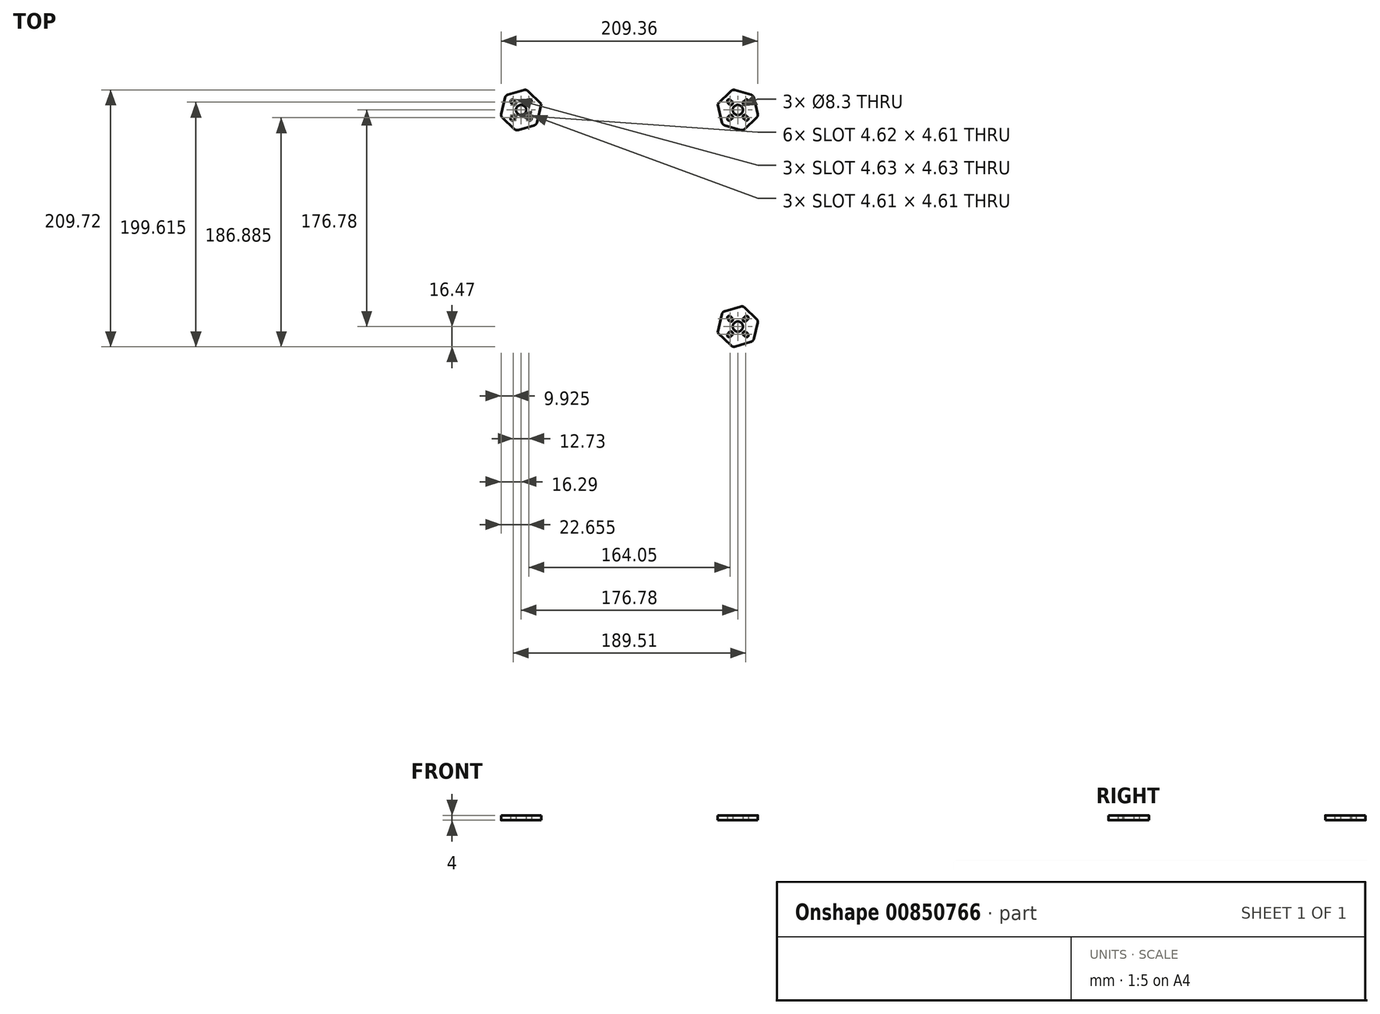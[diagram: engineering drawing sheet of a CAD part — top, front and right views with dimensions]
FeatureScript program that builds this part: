
annotation { "Feature Type Name" : "Feature", "Feature Type Description" : "" }
export const myFeature = defineFeature(function(context is Context, id is Id, definition is map)
    precondition{}
    {
        {
            var Q0;
            Q0=qCreatedBy(makeId("Top.planeOp"),FACE);
            var sketch = newSketch(context, id + "F0", { "sketchPlane" : qUnion([Q0])});
            skCircle(sketch, "E0", {"center": v(15.25, 15.25) * mm, "radius": 1.6 * mm});
            skPoint(sketch, "E1.middle", {"position": v(88.39, 88.39) * mm});
            skLineSegment(sketch, "E2", {"start": v(88.39, 88.39) * mm, "end": v(0, 0) * mm, "construction": true});
            skCircle(sketch, "E3", {"center": v(88.39, 88.39) * mm, "radius": 70 * mm, "construction": true});
            skLineSegment(sketch, "E4.MirrorCS", {"start": v(18.44, 10) * mm, "end": v(18.44, 0) * mm});
            skCircle(sketch, "E5", {"center": v(88.39, 88.39) * mm, "radius": 4.15 * mm});
            skLineSegment(sketch, "E6", {"start": v(5, 29.83) * mm, "end": v(84.33, 105.23) * mm});
            skCircle(sketch, "E7.cCircle", {"center": v(88.39, 88.39) * mm, "radius": 15 * mm, "construction": true});
            skLineSegment(sketch, "E7.0", {"start": v(71.78, 93.3) * mm, "end": v(84.33, 105.23) * mm});
            skLineSegment(sketch, "E7.1", {"start": v(84.33, 105.23) * mm, "end": v(100.94, 100.32) * mm});
            skLineSegment(sketch, "E7.2", {"start": v(100.94, 100.32) * mm, "end": v(105, 83.48) * mm});
            skLineSegment(sketch, "E7.3", {"start": v(105, 83.48) * mm, "end": v(92.44, 71.55) * mm});
            skLineSegment(sketch, "E7.4", {"start": v(92.44, 71.55) * mm, "end": v(75.83, 76.46) * mm});
            skLineSegment(sketch, "E7.5", {"start": v(75.83, 76.46) * mm, "end": v(71.78, 93.3) * mm});
            skPoint(sketch, "E7.0.midPoint", {"position": v(78.05, 99.26) * mm});
            skLineSegment(sketch, "E8", {"start": v(18.44, 0) * mm, "end": v(0, 0) * mm});
            skCircle(sketch, "E9.MirrorC", {"center": v(88.39, -88.39) * mm, "radius": 70 * mm, "construction": true});
            skLineSegment(sketch, "E10", {"start": v(22.44, 10) * mm, "end": v(22.44, 0) * mm});
            skLineSegment(sketch, "E11", {"start": v(22.44, 0) * mm, "end": v(31, 0) * mm});
            skLineSegment(sketch, "E12", {"start": v(31, 0) * mm, "end": v(31, 20) * mm});
            skCircle(sketch, "E13.MirrorC", {"center": v(-88.39, 88.39) * mm, "radius": 70 * mm, "construction": true});
            skCircle(sketch, "E14.MirrorC", {"center": v(-88.39, -88.39) * mm, "radius": 70 * mm, "construction": true});
            skLineSegment(sketch, "E15", {"start": v(22.44, 10) * mm, "end": v(18.44, 10) * mm, "construction": true});
            skArc(sketch, "E16", {"start": v(22.44, 10) * mm, "mid": v(20.44, 12) * mm, "end": v(18.44, 10) * mm});
            skLineSegment(sketch, "E17", {"start": v(5, 29.83) * mm, "end": v(0, 29.83) * mm});
            skLineSegment(sketch, "E18", {"start": v(0, 0) * mm, "end": v(0, 29.83) * mm});
            skCircle(sketch, "E19", {"center": v(28, 17) * mm, "radius": 1.65 * mm});
            skLineSegment(sketch, "E20", {"start": v(28, 17) * mm, "end": v(31, 17) * mm, "construction": true});
            skLineSegment(sketch, "E21", {"start": v(31, 17) * mm, "end": v(31, 20) * mm, "construction": true});
            skLineSegment(sketch, "E22", {"start": v(31, 17) * mm, "end": v(31, 20) * mm});
            skLineSegment(sketch, "E23", {"start": v(4.87, 0) * mm, "end": v(4.87, 10) * mm});
            skLineSegment(sketch, "E24", {"start": v(8.87, 0) * mm, "end": v(8.87, 10) * mm});
            skLineSegment(sketch, "E25", {"start": v(8.87, 10) * mm, "end": v(4.87, 10) * mm, "construction": true});
            skArc(sketch, "E26", {"start": v(8.87, 10) * mm, "mid": v(6.87, 12) * mm, "end": v(4.87, 10) * mm});
            skLineSegment(sketch, "E27", {"start": v(31, 20) * mm, "end": v(36.02, 33.1) * mm});
            skLineSegment(sketch, "E28", {"start": v(36.02, 33.1) * mm, "end": v(80.26, 75.15) * mm});
            skLineSegment(sketch, "E29.bottom", {"start": v(25, 14) * mm, "end": v(31, 14) * mm, "construction": true});
            skLineSegment(sketch, "E29.top", {"start": v(25, 20) * mm, "end": v(31, 20) * mm, "construction": true});
            skLineSegment(sketch, "E29.left", {"start": v(25, 14) * mm, "end": v(25, 20) * mm, "construction": true});
            skLineSegment(sketch, "E29.right", {"start": v(31, 14) * mm, "end": v(31, 20) * mm, "construction": true});
            skLineSegment(sketch, "E30", {"start": v(22.44, 0) * mm, "end": v(18.44, 0) * mm, "construction": true});
            skLineSegment(sketch, "E31", {"start": v(88.39, 88.39) * mm, "end": v(95.46, 81.32) * mm, "construction": true});
            skLineSegment(sketch, "E32", {"start": v(88.39, 88.39) * mm, "end": v(95.46, 95.46) * mm, "construction": true});
            skLineSegment(sketch, "E33", {"start": v(95.46, 95.46) * mm, "end": v(81.32, 81.32) * mm, "construction": true});
            skArc(sketch, "E34", {"start": v(96.6, 94.33) * mm, "mid": v(96.6, 96.6) * mm, "end": v(94.33, 96.6) * mm});
            skLineSegment(sketch, "E35", {"start": v(88.39, 88.39) * mm, "end": v(94.05, 94.05) * mm});
            skArc(sketch, "E36", {"start": v(92.91, 95.18) * mm, "mid": v(92.91, 92.91) * mm, "end": v(95.18, 92.91) * mm});
            skLineSegment(sketch, "E37", {"start": v(94.05, 94.05) * mm, "end": v(95.18, 92.91) * mm, "construction": true});
            skLineSegment(sketch, "E38", {"start": v(95.46, 95.46) * mm, "end": v(96.6, 94.33) * mm, "construction": true});
            skLineSegment(sketch, "E39", {"start": v(96.6, 94.33) * mm, "end": v(94.33, 96.6) * mm, "construction": true});
            skLineSegment(sketch, "E40", {"start": v(94.05, 94.05) * mm, "end": v(92.91, 95.18) * mm, "construction": true});
            skLineSegment(sketch, "E41", {"start": v(94.33, 96.6) * mm, "end": v(92.91, 95.18) * mm});
            skLineSegment(sketch, "E42", {"start": v(96.6, 94.33) * mm, "end": v(95.18, 92.91) * mm});
            skLineSegment(sketch, "E43", {"start": v(88.39, 88.39) * mm, "end": v(98.48, 88.39) * mm, "construction": true});
            skLineSegment(sketch, "E44", {"start": v(88.39, 88.39) * mm, "end": v(82.4, 88.39) * mm, "construction": true});
            skLineSegment(sketch, "E45", {"start": v(88.39, 88.39) * mm, "end": v(88.39, 82.43) * mm, "construction": true});
            skArc(sketch, "E46.MirrorCS", {"start": v(92.91, 81.6) * mm, "mid": v(92.91, 83.86) * mm, "end": v(95.18, 83.86) * mm});
            skArc(sketch, "E47.MirrorCS", {"start": v(96.6, 82.45) * mm, "mid": v(96.6, 80.19) * mm, "end": v(94.33, 80.19) * mm});
            skLineSegment(sketch, "E48.MirrorCS", {"start": v(94.33, 80.19) * mm, "end": v(92.91, 81.6) * mm});
            skLineSegment(sketch, "E49.MirrorCS", {"start": v(94.05, 82.73) * mm, "end": v(92.91, 81.6) * mm, "construction": true});
            skLineSegment(sketch, "E50.MirrorCS", {"start": v(95.46, 81.32) * mm, "end": v(96.6, 82.45) * mm, "construction": true});
            skLineSegment(sketch, "E51.MirrorCS", {"start": v(94.05, 82.73) * mm, "end": v(95.18, 83.86) * mm, "construction": true});
            skLineSegment(sketch, "E52.MirrorCS", {"start": v(96.6, 82.45) * mm, "end": v(94.33, 80.19) * mm, "construction": true});
            skLineSegment(sketch, "E53.MirrorCS", {"start": v(96.6, 82.45) * mm, "end": v(95.18, 83.86) * mm});
            skLineSegment(sketch, "E54.MirrorCS", {"start": v(80.19, 82.45) * mm, "end": v(81.6, 83.86) * mm});
            skLineSegment(sketch, "E55.MirrorCS", {"start": v(82.45, 80.19) * mm, "end": v(83.86, 81.6) * mm});
            skArc(sketch, "E56.MirrorCS", {"start": v(80.19, 82.45) * mm, "mid": v(80.19, 80.19) * mm, "end": v(82.45, 80.19) * mm});
            skArc(sketch, "E57.MirrorCS", {"start": v(83.86, 81.6) * mm, "mid": v(83.86, 83.86) * mm, "end": v(81.6, 83.86) * mm});
            skLineSegment(sketch, "E58.MirrorCS", {"start": v(80.19, 94.33) * mm, "end": v(81.6, 92.91) * mm});
            skLineSegment(sketch, "E59.MirrorCS", {"start": v(82.45, 96.6) * mm, "end": v(83.86, 95.18) * mm});
            skArc(sketch, "E60.MirrorCS", {"start": v(83.86, 95.18) * mm, "mid": v(83.86, 92.91) * mm, "end": v(81.6, 92.91) * mm});
            skArc(sketch, "E61.MirrorCS", {"start": v(80.19, 94.33) * mm, "mid": v(80.19, 96.6) * mm, "end": v(82.45, 96.6) * mm});
            skSolve(sketch);
        }
        {
            var Q0;
            Q0=makeQuery(id+"F0.imprint","IMPRINT",FACE,{"disambiguationData":[TD([[makeQuery(id+"F0.imprint","IMPRINT",EDGE,{"derivedFrom":sQuery(id+"F0.wireOp",EDGE,"E0")}),-1.0]])]});
            var Q1;
            Q1=makeQuery(id+"F0.imprint","IMPRINT",FACE,{"disambiguationData":[TD([[makeQuery(id+"F0.imprint","IMPRINT",EDGE,{"derivedFrom":sQuery(id+"F0.wireOp",EDGE,"a8402e06-ee66-4db1-b534-accf88d6755370.MirrorCS")}),1.0]])]});
            var Q2;
            Q2=makeQuery(id+"F0.imprint","IMPRINT",FACE,{"disambiguationData":[TD([[makeQuery(id+"F0.imprint","IMPRINT",EDGE,{"derivedFrom":sQuery(id+"F0.wireOp",EDGE,"E7.0")}),-1.0]])]});
            extrude(context, id + "F1", {"entities" : qUnion([Q0, Q1, Q2]), "depth" : 4 * mm, "offsetDistance" : 25 * mm});
        }
        {
            var Q0;
            Q0=makeQuery(id+"F1.opExtrude","SWEPT_EDGE",EDGE,{"disambiguationData":[OSD([sQuery(id+"F0.wireOp",EDGE,"E4.MirrorCS"),sQuery(id+"F0.wireOp",EDGE,"E16")])]});
            var Q1;
            Q1=makeQuery(id+"F1.opExtrude","SWEPT_EDGE",EDGE,{"disambiguationData":[OSD([sQuery(id+"F0.wireOp",EDGE,"cHvUN8nU-x71g-40xa-NfZp-NOtcJyjpFuAi"),sQuery(id+"F0.wireOp",EDGE,"epl4RrYL-OSQW-atUW-LyBx-qaYWwqfy6PMm")])]});
            var Q2;
            Q2=makeQuery(id+"F1.opExtrude","SWEPT_EDGE",EDGE,{"disambiguationData":[OSD([sQuery(id+"F0.wireOp",EDGE,"cHvUN8nU-x71g-40xa-NfZp-NOtcJyjpFuAi"),sQuery(id+"F0.wireOp",EDGE,"E7.4")])]});
            var Q3;
            Q3=makeQuery(id+"F1.opExtrude","SWEPT_EDGE",EDGE,{"disambiguationData":[OSD([sQuery(id+"F0.wireOp",EDGE,"E7.3"),sQuery(id+"F0.wireOp",EDGE,"E7.4")])]});
            var Q4;
            Q4=makeQuery(id+"F1.opExtrude","SWEPT_EDGE",EDGE,{"disambiguationData":[OSD([sQuery(id+"F0.wireOp",EDGE,"E7.2"),sQuery(id+"F0.wireOp",EDGE,"E7.3")])]});
            var Q5;
            Q5=makeQuery(id+"F1.opExtrude","SWEPT_EDGE",EDGE,{"disambiguationData":[OSD([sQuery(id+"F0.wireOp",EDGE,"E7.1"),sQuery(id+"F0.wireOp",EDGE,"E7.2")])]});
            var Q6;
            Q6=makeQuery(id+"F1.opExtrude","SWEPT_EDGE",EDGE,{"disambiguationData":[OSD([sQuery(id+"F0.wireOp",EDGE,"E7.0"),sQuery(id+"F0.wireOp",EDGE,"E7.1")])]});
            var Q7;
            Q7=makeQuery(id+"F1.opExtrude","SWEPT_EDGE",EDGE,{"disambiguationData":[OSD([sQuery(id+"F0.wireOp",EDGE,"E6"),sQuery(id+"F0.wireOp",EDGE,"E17")])]});
            var Q8;
            Q8=makeQuery(id+"F1.opExtrude","SWEPT_EDGE",EDGE,{"disambiguationData":[OSD([sQuery(id+"F0.wireOp",EDGE,"E27"),sQuery(id+"F0.wireOp",EDGE,"E28")])]});
            fillet(context, id + "F2", {"entities" : qUnion([Q0, Q1, Q2, Q3, Q4, Q5, Q6, Q7, Q8]), "radius" : 3 * mm, "tangentPropagation" : true, "allowEdgeOverflow" : false});
        }
        {
            var Q0;
            Q0=makeQuery(id+"F1.opExtrude","SWEPT_BODY",BODY,{"disambiguationData":[OSD([sQuery(id+"F0.wireOp",EDGE,"E0"),sQuery(id+"F0.wireOp",EDGE,"oWdG6ISu-KMsr-k3RM-oKNs-BBQdvasnS4HI"),sQuery(id+"F0.wireOp",EDGE,"5BciHUZ9-YItP-bftD-ryj1-fLEm0wkKDPWy"),sQuery(id+"F0.wireOp",EDGE,"IMcl1Ms8-7Su7-6ZAW-NG62-JrzNrDPbqV1x"),sQuery(id+"F0.wireOp",EDGE,"9lDLXxTV-PYSm-tJxw-fFQl-kT38rdbVkR7x"),sQuery(id+"F0.wireOp",EDGE,"BTfzHgYM-Pcws-li4g-SYp3-UJARv1mQOSm9"),sQuery(id+"F0.wireOp",EDGE,"db9e6dd7-a62a-4760-a6cd-ab0fbc12ccb50.MirrorCS"),sQuery(id+"F0.wireOp",EDGE,"E4.MirrorCS"),sQuery(id+"F0.wireOp",EDGE,"E5"),sQuery(id+"F0.wireOp",EDGE,"cHvUN8nU-x71g-40xa-NfZp-NOtcJyjpFuAi"),sQuery(id+"F0.wireOp",EDGE,"0RzsWIGJ-paQ4-ph2x-eddI-tqWgFJrQCAKC"),sQuery(id+"F0.wireOp",EDGE,"a8402e06-ee66-4db1-b534-accf88d6755370.MirrorCS"),sQuery(id+"F0.wireOp",EDGE,"b02bcf13-f754-48f6-a3d9-f9d052b593f50.MirrorCS"),sQuery(id+"F0.wireOp",EDGE,"694f7e91-0505-4e5e-88bd-36493d61fdc10.MirrorCS"),sQuery(id+"F0.wireOp",EDGE,"c5342205-c0ba-4404-b584-cfb84c0711390.MirrorCS"),sQuery(id+"F0.wireOp",EDGE,"41230d2a-ef97-414e-a6b5-391d20fd2f8c0.MirrorCS"),sQuery(id+"F0.wireOp",EDGE,"f38d681c-4026-4150-9bb3-d62f81ecb60f0.MirrorCS"),sQuery(id+"F0.wireOp",EDGE,"f9c18b0d-e090-48c1-8617-159294224c630.MirrorCS"),sQuery(id+"F0.wireOp",EDGE,"00e02f4d-f463-4009-913d-c35542a66ec00.MirrorCS"),sQuery(id+"F0.wireOp",EDGE,"3930c83d-3c26-45a6-b419-dbd5f18dbc8c0.MirrorCS"),sQuery(id+"F0.wireOp",EDGE,"795dee3e-9adc-4518-a6c0-085d1af0c0d60.MirrorCS"),sQuery(id+"F0.wireOp",EDGE,"679d401b-33ac-4602-9026-ff56514631890.MirrorCS"),sQuery(id+"F0.wireOp",EDGE,"5c1dbbd6-dfe0-41fd-a57b-e75cf78051b50.MirrorCS"),sQuery(id+"F0.wireOp",EDGE,"7f1d194b-443a-46c3-ae38-eac5abfad72a0.MirrorCS"),sQuery(id+"F0.wireOp",EDGE,"7f1d194b-443a-46c3-ae38-eac5abfad72a1.MirrorCS"),sQuery(id+"F0.wireOp",EDGE,"7f1d194b-443a-46c3-ae38-eac5abfad72a2.MirrorCS"),sQuery(id+"F0.wireOp",EDGE,"7f1d194b-443a-46c3-ae38-eac5abfad72a3.MirrorCS"),sQuery(id+"F0.wireOp",EDGE,"7f1d194b-443a-46c3-ae38-eac5abfad72a4.MirrorCS"),sQuery(id+"F0.wireOp",EDGE,"7f1d194b-443a-46c3-ae38-eac5abfad72a5.MirrorCS"),sQuery(id+"F0.wireOp",EDGE,"9a7043b3-dbb6-42aa-b538-a97c510add320.MirrorCS"),sQuery(id+"F0.wireOp",EDGE,"9a7043b3-dbb6-42aa-b538-a97c510add321.MirrorCS"),sQuery(id+"F0.wireOp",EDGE,"9a7043b3-dbb6-42aa-b538-a97c510add322.MirrorCS"),sQuery(id+"F0.wireOp",EDGE,"9a7043b3-dbb6-42aa-b538-a97c510add323.MirrorCS"),sQuery(id+"F0.wireOp",EDGE,"9a7043b3-dbb6-42aa-b538-a97c510add324.MirrorCS"),sQuery(id+"F0.wireOp",EDGE,"9a7043b3-dbb6-42aa-b538-a97c510add325.MirrorCS"),sQuery(id+"F0.wireOp",EDGE,"FqZT0Coj-QeVh-UZiT-ubz3-8URiVkSl8LEo"),sQuery(id+"F0.wireOp",EDGE,"E6"),sQuery(id+"F0.wireOp",EDGE,"E7.0"),sQuery(id+"F0.wireOp",EDGE,"E7.1"),sQuery(id+"F0.wireOp",EDGE,"E7.2"),sQuery(id+"F0.wireOp",EDGE,"E7.3"),sQuery(id+"F0.wireOp",EDGE,"E7.4"),sQuery(id+"F0.wireOp",EDGE,"sgrcP4Hu-TaEZ-ddCh-wFjH-NDSiAUyIGktv"),sQuery(id+"F0.wireOp",EDGE,"yxbqhxj4-Hobq-MuBO-747H-CFA98GxcXYLo"),sQuery(id+"F0.wireOp",EDGE,"E8"),sQuery(id+"F0.wireOp",EDGE,"GbNPMmSl-UyhI-VWxR-HjZI-7ZSacyFRmm5m"),sQuery(id+"F0.wireOp",EDGE,"380TYFXR-L58P-DwUR-NOKN-1QwqNV3a178d")])]});
            var Q1;
            Q1=qCreatedBy(makeId("Right.planeOp"),FACE);
            mirror(context, id + "F3", {"operationType" : NewBodyOperationType.ADD, "entities" : qUnion([Q0]), "mirrorPlane" : qUnion([Q1])});
        }
        {
            var Q0;
            Q0=makeQuery(id+"F1.opExtrude","SWEPT_BODY",BODY,{"disambiguationData":[OSD([sQuery(id+"F0.wireOp",EDGE,"E0"),sQuery(id+"F0.wireOp",EDGE,"oWdG6ISu-KMsr-k3RM-oKNs-BBQdvasnS4HI"),sQuery(id+"F0.wireOp",EDGE,"5BciHUZ9-YItP-bftD-ryj1-fLEm0wkKDPWy"),sQuery(id+"F0.wireOp",EDGE,"IMcl1Ms8-7Su7-6ZAW-NG62-JrzNrDPbqV1x"),sQuery(id+"F0.wireOp",EDGE,"9lDLXxTV-PYSm-tJxw-fFQl-kT38rdbVkR7x"),sQuery(id+"F0.wireOp",EDGE,"BTfzHgYM-Pcws-li4g-SYp3-UJARv1mQOSm9"),sQuery(id+"F0.wireOp",EDGE,"db9e6dd7-a62a-4760-a6cd-ab0fbc12ccb50.MirrorCS"),sQuery(id+"F0.wireOp",EDGE,"E4.MirrorCS"),sQuery(id+"F0.wireOp",EDGE,"E5"),sQuery(id+"F0.wireOp",EDGE,"cHvUN8nU-x71g-40xa-NfZp-NOtcJyjpFuAi"),sQuery(id+"F0.wireOp",EDGE,"0RzsWIGJ-paQ4-ph2x-eddI-tqWgFJrQCAKC"),sQuery(id+"F0.wireOp",EDGE,"a8402e06-ee66-4db1-b534-accf88d6755370.MirrorCS"),sQuery(id+"F0.wireOp",EDGE,"b02bcf13-f754-48f6-a3d9-f9d052b593f50.MirrorCS"),sQuery(id+"F0.wireOp",EDGE,"694f7e91-0505-4e5e-88bd-36493d61fdc10.MirrorCS"),sQuery(id+"F0.wireOp",EDGE,"c5342205-c0ba-4404-b584-cfb84c0711390.MirrorCS"),sQuery(id+"F0.wireOp",EDGE,"41230d2a-ef97-414e-a6b5-391d20fd2f8c0.MirrorCS"),sQuery(id+"F0.wireOp",EDGE,"f38d681c-4026-4150-9bb3-d62f81ecb60f0.MirrorCS"),sQuery(id+"F0.wireOp",EDGE,"f9c18b0d-e090-48c1-8617-159294224c630.MirrorCS"),sQuery(id+"F0.wireOp",EDGE,"00e02f4d-f463-4009-913d-c35542a66ec00.MirrorCS"),sQuery(id+"F0.wireOp",EDGE,"3930c83d-3c26-45a6-b419-dbd5f18dbc8c0.MirrorCS"),sQuery(id+"F0.wireOp",EDGE,"795dee3e-9adc-4518-a6c0-085d1af0c0d60.MirrorCS"),sQuery(id+"F0.wireOp",EDGE,"679d401b-33ac-4602-9026-ff56514631890.MirrorCS"),sQuery(id+"F0.wireOp",EDGE,"5c1dbbd6-dfe0-41fd-a57b-e75cf78051b50.MirrorCS"),sQuery(id+"F0.wireOp",EDGE,"7f1d194b-443a-46c3-ae38-eac5abfad72a0.MirrorCS"),sQuery(id+"F0.wireOp",EDGE,"7f1d194b-443a-46c3-ae38-eac5abfad72a1.MirrorCS"),sQuery(id+"F0.wireOp",EDGE,"7f1d194b-443a-46c3-ae38-eac5abfad72a2.MirrorCS"),sQuery(id+"F0.wireOp",EDGE,"7f1d194b-443a-46c3-ae38-eac5abfad72a3.MirrorCS"),sQuery(id+"F0.wireOp",EDGE,"7f1d194b-443a-46c3-ae38-eac5abfad72a4.MirrorCS"),sQuery(id+"F0.wireOp",EDGE,"7f1d194b-443a-46c3-ae38-eac5abfad72a5.MirrorCS"),sQuery(id+"F0.wireOp",EDGE,"9a7043b3-dbb6-42aa-b538-a97c510add320.MirrorCS"),sQuery(id+"F0.wireOp",EDGE,"9a7043b3-dbb6-42aa-b538-a97c510add321.MirrorCS"),sQuery(id+"F0.wireOp",EDGE,"9a7043b3-dbb6-42aa-b538-a97c510add322.MirrorCS"),sQuery(id+"F0.wireOp",EDGE,"9a7043b3-dbb6-42aa-b538-a97c510add323.MirrorCS"),sQuery(id+"F0.wireOp",EDGE,"9a7043b3-dbb6-42aa-b538-a97c510add324.MirrorCS"),sQuery(id+"F0.wireOp",EDGE,"9a7043b3-dbb6-42aa-b538-a97c510add325.MirrorCS"),sQuery(id+"F0.wireOp",EDGE,"FqZT0Coj-QeVh-UZiT-ubz3-8URiVkSl8LEo"),sQuery(id+"F0.wireOp",EDGE,"E6"),sQuery(id+"F0.wireOp",EDGE,"E7.0"),sQuery(id+"F0.wireOp",EDGE,"E7.1"),sQuery(id+"F0.wireOp",EDGE,"E7.2"),sQuery(id+"F0.wireOp",EDGE,"E7.3"),sQuery(id+"F0.wireOp",EDGE,"E7.4"),sQuery(id+"F0.wireOp",EDGE,"sgrcP4Hu-TaEZ-ddCh-wFjH-NDSiAUyIGktv"),sQuery(id+"F0.wireOp",EDGE,"yxbqhxj4-Hobq-MuBO-747H-CFA98GxcXYLo"),sQuery(id+"F0.wireOp",EDGE,"E8"),sQuery(id+"F0.wireOp",EDGE,"GbNPMmSl-UyhI-VWxR-HjZI-7ZSacyFRmm5m"),sQuery(id+"F0.wireOp",EDGE,"380TYFXR-L58P-DwUR-NOKN-1QwqNV3a178d")])]});
            var Q1;
            Q1=qCreatedBy(makeId("Front.planeOp"),FACE);
            mirror(context, id + "F4", {"operationType" : NewBodyOperationType.ADD, "entities" : qUnion([Q0]), "mirrorPlane" : qUnion([Q1])});
        }
    });
